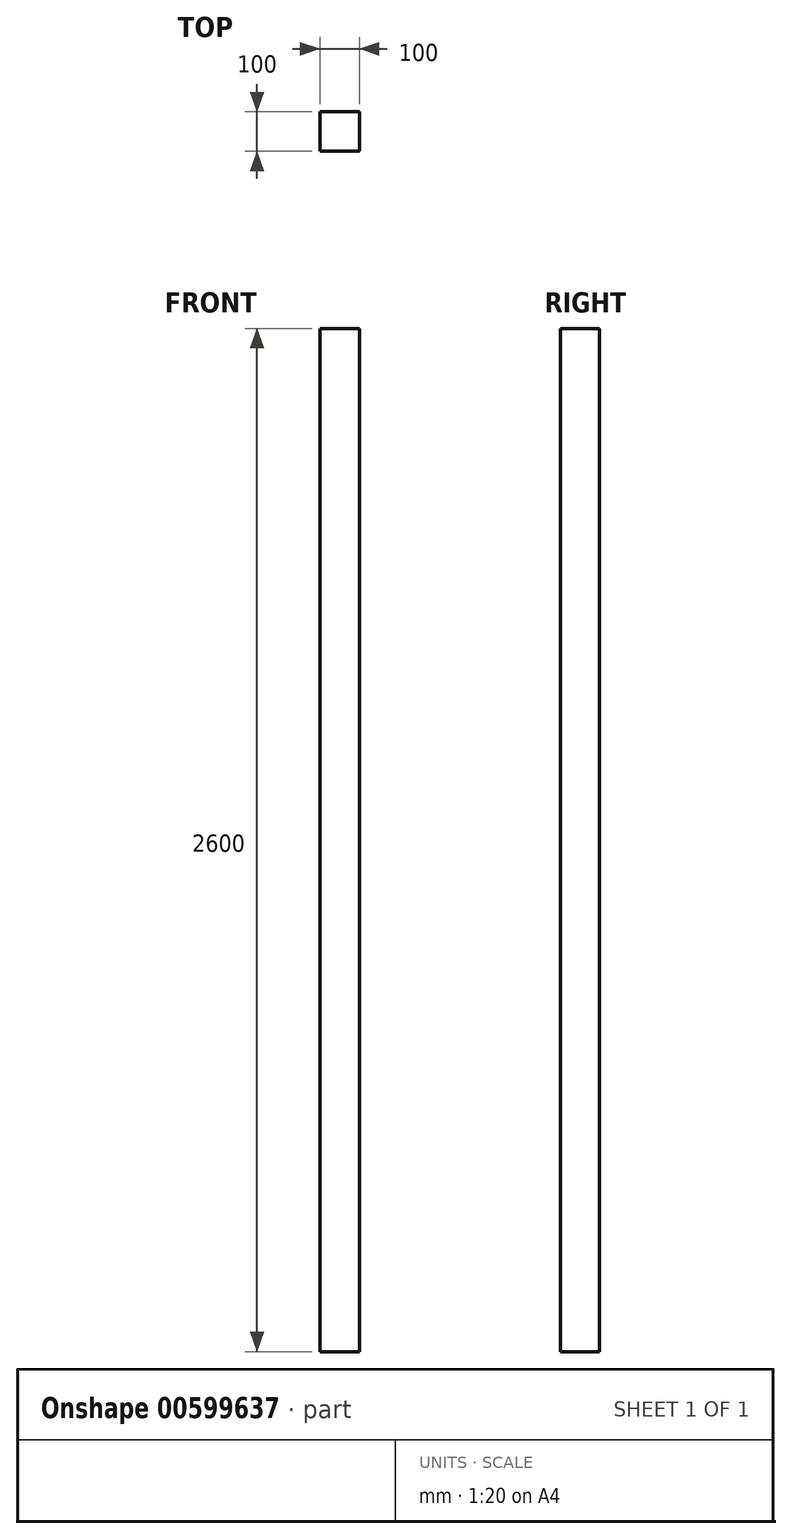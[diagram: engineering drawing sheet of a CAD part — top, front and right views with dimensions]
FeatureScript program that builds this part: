
annotation { "Feature Type Name" : "Feature", "Feature Type Description" : "" }
export const myFeature = defineFeature(function(context is Context, id is Id, definition is map)
    precondition{}
    {
        {
            var Q0;
            Q0=qCreatedBy(makeId("Top.planeOp"),FACE);
            var sketch = newSketch(context, id + "F0", { "sketchPlane" : qUnion([Q0])});
            skLineSegment(sketch, "E0.bottom", {"start": v(-50, -50) * mm, "end": v(50, -50) * mm});
            skLineSegment(sketch, "E0.top", {"start": v(-50, 50) * mm, "end": v(50, 50) * mm});
            skLineSegment(sketch, "E0.left", {"start": v(-50, -50) * mm, "end": v(-50, 50) * mm});
            skLineSegment(sketch, "E0.right", {"start": v(50, -50) * mm, "end": v(50, 50) * mm});
            skPoint(sketch, "E0.middle", {"position": v(0, 0) * mm});
            skSolve(sketch);
        }
        {
            var Q0;
            Q0 = qSketchRegion(id + "F0", true);
            extrude(context, id + "F1", {"entities" : qUnion([Q0]), "depth" : 2600 * mm, "offsetDistance" : 25 * mm});
        }
    });
